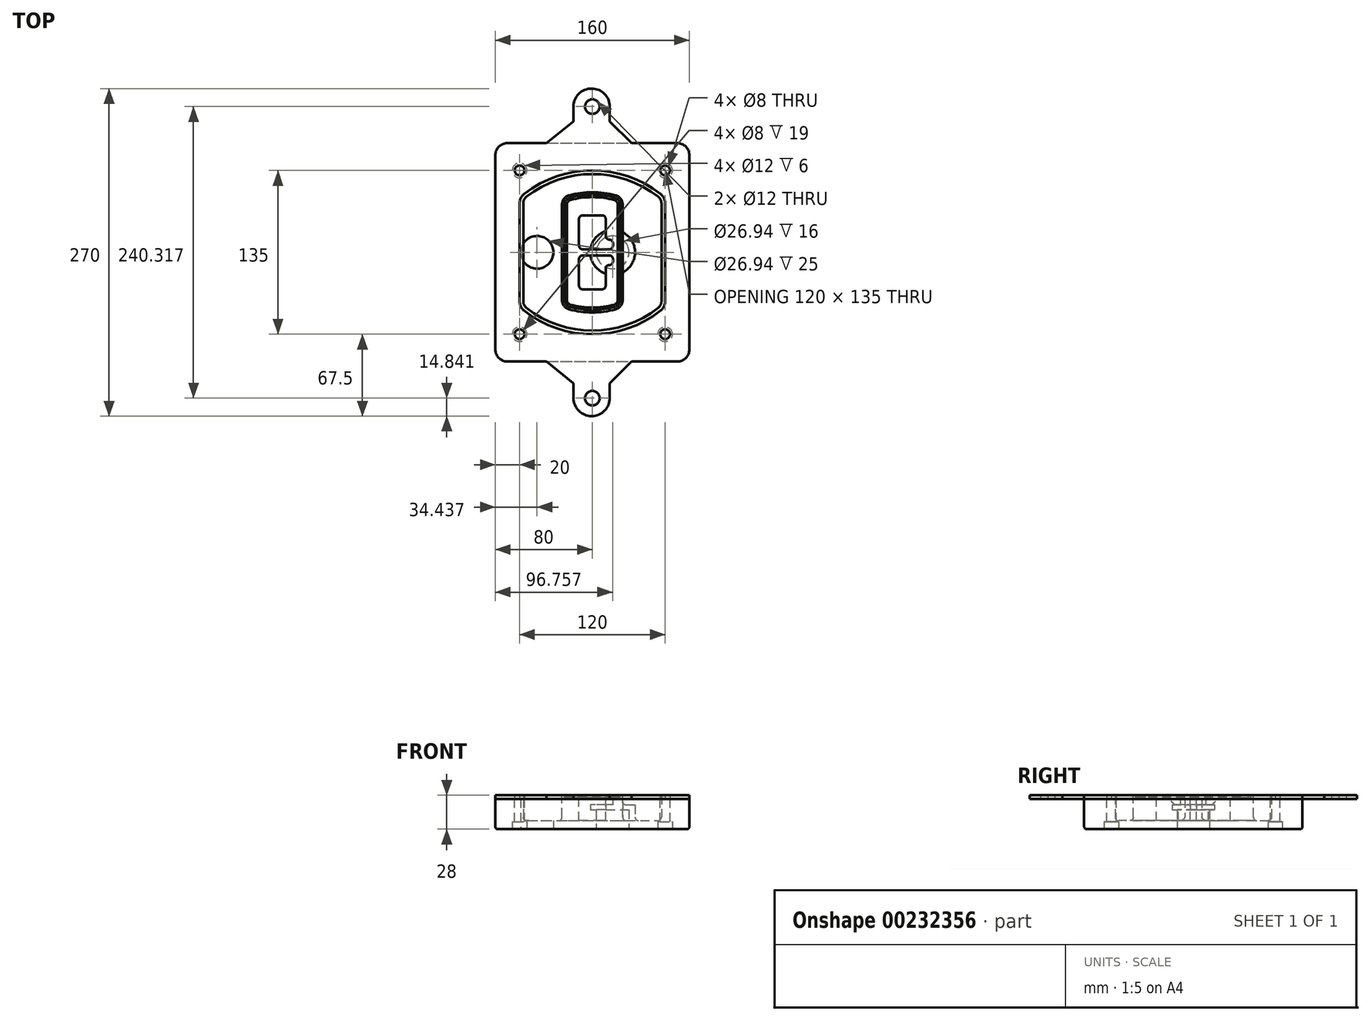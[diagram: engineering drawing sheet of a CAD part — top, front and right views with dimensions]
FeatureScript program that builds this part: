
annotation { "Feature Type Name" : "Feature", "Feature Type Description" : "" }
export const myFeature = defineFeature(function(context is Context, id is Id, definition is map)
    precondition{}
    {
        {
            var Q0;
            Q0=qCreatedBy(makeId("Top.planeOp"),FACE);
            var sketch = newSketch(context, id + "F0", { "sketchPlane" : qUnion([Q0])});
            skPoint(sketch, "E0.rect.middle", {"position": v(0, 0) * mm});
            skLineSegment(sketch, "E1.bottom", {"start": v(-70, -90) * mm, "end": v(70, -90) * mm});
            skLineSegment(sketch, "E1.top", {"start": v(-70, 90) * mm, "end": v(70, 90) * mm});
            skLineSegment(sketch, "E1.left", {"start": v(-80, -80) * mm, "end": v(-80, 80) * mm});
            skLineSegment(sketch, "E1.right", {"start": v(80, -80) * mm, "end": v(80, 80) * mm});
            skLineSegment(sketch, "E2", {"start": v(-80, 90) * mm, "end": v(80, -90) * mm, "construction": true});
            skLineSegment(sketch, "E3", {"start": v(80, 90) * mm, "end": v(-80, -90) * mm, "construction": true});
            skCircle(sketch, "E4", {"center": v(-60, 67.5) * mm, "radius": 4 * mm});
            skCircle(sketch, "E5", {"center": v(60, 67.5) * mm, "radius": 4 * mm});
            skCircle(sketch, "E6", {"center": v(60, -67.5) * mm, "radius": 4 * mm});
            skCircle(sketch, "E7", {"center": v(-60, -67.5) * mm, "radius": 4 * mm});
            skLineSegment(sketch, "E8", {"start": v(-60, 67.5) * mm, "end": v(60, 67.5) * mm, "construction": true});
            skLineSegment(sketch, "E9", {"start": v(60, 67.5) * mm, "end": v(60, -67.5) * mm, "construction": true});
            skLineSegment(sketch, "E10", {"start": v(60, -67.5) * mm, "end": v(-60, -67.5) * mm, "construction": true});
            skLineSegment(sketch, "E11", {"start": v(-60, -67.5) * mm, "end": v(-60, 67.5) * mm, "construction": true});
            skLineSegment(sketch, "E12", {"start": v(-60, 40.3) * mm, "end": v(-60, -40.3) * mm});
            skLineSegment(sketch, "E13", {"start": v(60, 40.3) * mm, "end": v(60, -40.3) * mm});
            skArc(sketch, "E14", {"start": v(56.15, 48.18) * mm, "mid": v(0, 67.5) * mm, "end": v(-56.15, 48.18) * mm});
            skArc(sketch, "E15", {"start": v(-56.15, -48.18) * mm, "mid": v(0, -67.5) * mm, "end": v(56.15, -48.18) * mm});
            skLineSegment(sketch, "E16", {"start": v(-60, 0) * mm, "end": v(60, 0) * mm, "construction": true});
            skPoint(sketch, "E17.visualSharp", {"position": v(-60, -45) * mm});
            skArc(sketch, "E17.filletArc", {"start": v(-60, -40.3) * mm, "mid": v(-58.99, -44.68) * mm, "end": v(-56.15, -48.18) * mm});
            skPoint(sketch, "E18.visualSharp", {"position": v(-60, 45) * mm});
            skArc(sketch, "E18.filletArc", {"start": v(-56.15, 48.18) * mm, "mid": v(-58.99, 44.68) * mm, "end": v(-60, 40.3) * mm});
            skPoint(sketch, "E19.visualSharp", {"position": v(60, 45) * mm});
            skArc(sketch, "E19.filletArc", {"start": v(60, 40.3) * mm, "mid": v(58.99, 44.68) * mm, "end": v(56.15, 48.18) * mm});
            skPoint(sketch, "E20.visualSharp", {"position": v(60, -45) * mm});
            skArc(sketch, "E20.filletArc", {"start": v(56.15, -48.18) * mm, "mid": v(58.99, -44.68) * mm, "end": v(60, -40.3) * mm});
            skPoint(sketch, "E21.visualSharp", {"position": v(-80, 90) * mm});
            skArc(sketch, "E21.filletArc", {"start": v(-70, 90) * mm, "mid": v(-77.07, 87.07) * mm, "end": v(-80, 80) * mm});
            skPoint(sketch, "E22.visualSharp", {"position": v(80, 90) * mm});
            skArc(sketch, "E22.filletArc", {"start": v(80, 80) * mm, "mid": v(77.07, 87.07) * mm, "end": v(70, 90) * mm});
            skPoint(sketch, "E23.visualSharp", {"position": v(80, -90) * mm});
            skArc(sketch, "E23.filletArc", {"start": v(70, -90) * mm, "mid": v(77.07, -87.07) * mm, "end": v(80, -80) * mm});
            skPoint(sketch, "E24.visualSharp", {"position": v(-80, -90) * mm});
            skArc(sketch, "E24.filletArc", {"start": v(-80, -80) * mm, "mid": v(-77.07, -87.07) * mm, "end": v(-70, -90) * mm});
            skArc(sketch, "E25.0", {"start": v(57, 40.3) * mm, "mid": v(56.3, 43.36) * mm, "end": v(54.3, 45.81) * mm});
            skLineSegment(sketch, "E25.1", {"start": v(57, 40.3) * mm, "end": v(57, -40.3) * mm});
            skArc(sketch, "E25.2", {"start": v(54.3, -45.81) * mm, "mid": v(56.3, -43.36) * mm, "end": v(57, -40.3) * mm});
            skArc(sketch, "E25.3", {"start": v(-54.3, -45.81) * mm, "mid": v(0, -64.5) * mm, "end": v(54.3, -45.81) * mm});
            skArc(sketch, "E25.4", {"start": v(-57, -40.3) * mm, "mid": v(-56.3, -43.36) * mm, "end": v(-54.3, -45.81) * mm});
            skArc(sketch, "E25.5", {"start": v(54.3, 45.81) * mm, "mid": v(0, 64.5) * mm, "end": v(-54.3, 45.81) * mm});
            skLineSegment(sketch, "E25.6", {"start": v(-57, 40.3) * mm, "end": v(-57, -40.3) * mm});
            skArc(sketch, "E25.7", {"start": v(-54.3, 45.81) * mm, "mid": v(-56.3, 43.36) * mm, "end": v(-57, 40.3) * mm});
            skArc(sketch, "E26.0", {"start": v(-58.62, 51.33) * mm, "mid": v(-62.58, 46.43) * mm, "end": v(-64, 40.3) * mm});
            skArc(sketch, "E26.1", {"start": v(58.62, 51.33) * mm, "mid": v(0, 71.5) * mm, "end": v(-58.62, 51.33) * mm});
            skArc(sketch, "E26.2", {"start": v(64, 40.3) * mm, "mid": v(62.58, 46.43) * mm, "end": v(58.62, 51.33) * mm});
            skLineSegment(sketch, "E26.3", {"start": v(64, 40.3) * mm, "end": v(64, -40.3) * mm});
            skArc(sketch, "E26.4", {"start": v(58.62, -51.33) * mm, "mid": v(62.58, -46.43) * mm, "end": v(64, -40.3) * mm});
            skLineSegment(sketch, "E26.5", {"start": v(-64, 40.3) * mm, "end": v(-64, -40.3) * mm});
            skArc(sketch, "E26.6", {"start": v(-58.62, -51.33) * mm, "mid": v(0, -71.5) * mm, "end": v(58.62, -51.33) * mm});
            skArc(sketch, "E26.7", {"start": v(-64, -40.3) * mm, "mid": v(-62.58, -46.43) * mm, "end": v(-58.62, -51.33) * mm});
            skSolve(sketch);
        }
        {
            var Q0;
            Q0=makeQuery(id+"F0.imprint","IMPRINT",FACE,{"disambiguationData":[TD([[makeQuery(id+"F0.imprint","IMPRINT",EDGE,{"derivedFrom":sQuery(id+"F0.wireOp",EDGE,"E1.bottom")}),1.0]])]});
            var Q1;
            Q1=makeQuery(id+"F0.imprint","IMPRINT",FACE,{"disambiguationData":[TD([[makeQuery(id+"F0.imprint","IMPRINT",EDGE,{"derivedFrom":sQuery(id+"F0.wireOp",EDGE,"E12")}),1.0]])]});
            var Q2;
            Q2=makeQuery(id+"F0.imprint","IMPRINT",FACE,{"disambiguationData":[TD([[makeQuery(id+"F0.imprint","IMPRINT",EDGE,{"derivedFrom":sQuery(id+"F0.wireOp",EDGE,"E25.0")}),1.0]])]});
            var Q3;
            Q3=makeQuery(id+"F0.imprint","IMPRINT",FACE,{"disambiguationData":[TD([[makeQuery(id+"F0.imprint","IMPRINT",EDGE,{"derivedFrom":sQuery(id+"F0.wireOp",EDGE,"E12")}),-1.0]])]});
            extrude(context, id + "F1", {"entities" : qUnion([Q0, Q1, Q2, Q3]), "oppositeDirection" : true, "depth" : 25 * mm});
        }
        {
            var Q0;
            Q0=makeQuery(id+"F0.imprint","IMPRINT",FACE,{"disambiguationData":[TD([[makeQuery(id+"F0.imprint","IMPRINT",EDGE,{"derivedFrom":sQuery(id+"F0.wireOp",EDGE,"E12")}),1.0]])]});
            extrude(context, id + "F2", {"entities" : qUnion([Q0]), "operationType" : NewBodyOperationType.ADD, "depth" : 3 * mm});
        }
        {
            var Q0;
            Q0=makeQuery(id+"F0.imprint","IMPRINT",FACE,{"disambiguationData":[TD([[makeQuery(id+"F0.imprint","IMPRINT",EDGE,{"derivedFrom":sQuery(id+"F0.wireOp",EDGE,"E25.0")}),1.0]])]});
            extrude(context, id + "F3", {"entities" : qUnion([Q0]), "operationType" : NewBodyOperationType.REMOVE, "oppositeDirection" : true, "depth" : 18 * mm});
        }
        {
            var Q0;
            Q0=makeQuery(id+"F2.opExtrude","CAP_FACE",FACE,{"disambiguationData":[OSD([sQuery(id+"F0.wireOp",EDGE,"E12"),sQuery(id+"F0.wireOp",EDGE,"E13"),sQuery(id+"F0.wireOp",EDGE,"E14"),sQuery(id+"F0.wireOp",EDGE,"E15"),sQuery(id+"F0.wireOp",EDGE,"E17.filletArc"),sQuery(id+"F0.wireOp",EDGE,"E18.filletArc"),sQuery(id+"F0.wireOp",EDGE,"E19.filletArc"),sQuery(id+"F0.wireOp",EDGE,"E20.filletArc"),sQuery(id+"F0.wireOp",EDGE,"E25.0"),sQuery(id+"F0.wireOp",EDGE,"E25.1"),sQuery(id+"F0.wireOp",EDGE,"E25.2"),sQuery(id+"F0.wireOp",EDGE,"E25.3"),sQuery(id+"F0.wireOp",EDGE,"E25.4"),sQuery(id+"F0.wireOp",EDGE,"E25.5"),sQuery(id+"F0.wireOp",EDGE,"E25.6"),sQuery(id+"F0.wireOp",EDGE,"E25.7")])],"isStart":false});
            var sketch = newSketch(context, id + "F4", { "sketchPlane" : qUnion([Q0])});
            skArc(sketch, "E27.0", {"start": v(-19.08, -46.97) * mm, "mid": v(0, -49.5) * mm, "end": v(19.08, -46.97) * mm});
            skArc(sketch, "E28.0", {"start": v(19.08, 46.97) * mm, "mid": v(0, 49.5) * mm, "end": v(-19.08, 46.97) * mm});
            skLineSegment(sketch, "E29", {"start": v(-25, 39.25) * mm, "end": v(-25, -39.25) * mm});
            skLineSegment(sketch, "E30", {"start": v(25, 39.25) * mm, "end": v(25, -39.25) * mm});
            skLineSegment(sketch, "E31", {"start": v(-25, 45.1) * mm, "end": v(25, 45.1) * mm, "construction": true});
            skLineSegment(sketch, "E32", {"start": v(-25, -45.1) * mm, "end": v(25, -45.1) * mm, "construction": true});
            skPoint(sketch, "E33.visualSharp", {"position": v(-25, 45.1) * mm});
            skArc(sketch, "E33.filletArc", {"start": v(-19.08, 46.97) * mm, "mid": v(-23.35, 44.11) * mm, "end": v(-25, 39.25) * mm});
            skPoint(sketch, "E34.visualSharp", {"position": v(25, 45.1) * mm});
            skArc(sketch, "E34.filletArc", {"start": v(25, 39.25) * mm, "mid": v(23.35, 44.11) * mm, "end": v(19.08, 46.97) * mm});
            skPoint(sketch, "E35.visualSharp", {"position": v(25, -45.1) * mm});
            skArc(sketch, "E35.filletArc", {"start": v(19.08, -46.97) * mm, "mid": v(23.35, -44.11) * mm, "end": v(25, -39.25) * mm});
            skPoint(sketch, "E36.visualSharp", {"position": v(-25, -45.1) * mm});
            skArc(sketch, "E36.filletArc", {"start": v(-25, -39.25) * mm, "mid": v(-23.35, -44.11) * mm, "end": v(-19.08, -46.97) * mm});
            skArc(sketch, "E37.0", {"start": v(54.3, 45.81) * mm, "mid": v(0, 64.5) * mm, "end": v(-54.3, 45.81) * mm});
            skArc(sketch, "E37.1", {"start": v(-54.3, 45.81) * mm, "mid": v(-56.3, 43.36) * mm, "end": v(-57, 40.3) * mm});
            skLineSegment(sketch, "E37.2", {"start": v(-57, 40.3) * mm, "end": v(-57, -40.3) * mm});
            skArc(sketch, "E37.3", {"start": v(-57, -40.3) * mm, "mid": v(-56.3, -43.36) * mm, "end": v(-54.3, -45.81) * mm});
            skArc(sketch, "E37.4", {"start": v(-54.3, -45.81) * mm, "mid": v(0, -64.5) * mm, "end": v(54.3, -45.81) * mm});
            skArc(sketch, "E37.5", {"start": v(54.3, -45.81) * mm, "mid": v(56.3, -43.36) * mm, "end": v(57, -40.3) * mm});
            skLineSegment(sketch, "E37.6", {"start": v(57, 40.3) * mm, "end": v(57, -40.3) * mm});
            skArc(sketch, "E37.7", {"start": v(57, 40.3) * mm, "mid": v(56.3, 43.36) * mm, "end": v(54.3, 45.81) * mm});
            skLineSegment(sketch, "E38.0", {"start": v(23, 39.25) * mm, "end": v(23, -39.25) * mm});
            skArc(sketch, "E38.1", {"start": v(18.56, -45.04) * mm, "mid": v(21.76, -42.9) * mm, "end": v(23, -39.25) * mm});
            skArc(sketch, "E38.2", {"start": v(-18.56, -45.04) * mm, "mid": v(0, -47.5) * mm, "end": v(18.56, -45.04) * mm});
            skArc(sketch, "E38.3", {"start": v(-23, -39.25) * mm, "mid": v(-21.76, -42.9) * mm, "end": v(-18.56, -45.04) * mm});
            skLineSegment(sketch, "E38.4", {"start": v(-23, 39.25) * mm, "end": v(-23, -39.25) * mm});
            skArc(sketch, "E38.5", {"start": v(23, 39.25) * mm, "mid": v(21.76, 42.9) * mm, "end": v(18.56, 45.04) * mm});
            skArc(sketch, "E38.6", {"start": v(-18.56, 45.04) * mm, "mid": v(-21.76, 42.9) * mm, "end": v(-23, 39.25) * mm});
            skArc(sketch, "E38.7", {"start": v(18.56, 45.04) * mm, "mid": v(0, 47.5) * mm, "end": v(-18.56, 45.04) * mm});
            skArc(sketch, "E39.0", {"start": v(21, 39.25) * mm, "mid": v(20.18, 41.68) * mm, "end": v(18.04, 43.1) * mm});
            skLineSegment(sketch, "E39.1", {"start": v(21, 39.25) * mm, "end": v(21, -39.25) * mm});
            skArc(sketch, "E39.2", {"start": v(18.04, -43.1) * mm, "mid": v(20.18, -41.68) * mm, "end": v(21, -39.25) * mm});
            skArc(sketch, "E39.3", {"start": v(-18.04, -43.1) * mm, "mid": v(0, -45.5) * mm, "end": v(18.04, -43.1) * mm});
            skArc(sketch, "E39.4", {"start": v(-21, -39.25) * mm, "mid": v(-20.18, -41.68) * mm, "end": v(-18.04, -43.1) * mm});
            skArc(sketch, "E39.5", {"start": v(18.04, 43.1) * mm, "mid": v(0, 45.5) * mm, "end": v(-18.04, 43.1) * mm});
            skLineSegment(sketch, "E39.6", {"start": v(-21, 39.25) * mm, "end": v(-21, -39.25) * mm});
            skArc(sketch, "E39.7", {"start": v(-18.04, 43.1) * mm, "mid": v(-20.18, 41.68) * mm, "end": v(-21, 39.25) * mm});
            skLineSegment(sketch, "E40", {"start": v(-25, 0) * mm, "end": v(25, 0) * mm, "construction": true});
            skLineSegment(sketch, "E41", {"start": v(-11, 5.5) * mm, "end": v(-11, 27.5) * mm});
            skLineSegment(sketch, "E42", {"start": v(-8, 30.5) * mm, "end": v(8, 30.5) * mm});
            skLineSegment(sketch, "E43", {"start": v(11, 27.5) * mm, "end": v(11, 13.5) * mm});
            skLineSegment(sketch, "E44", {"start": v(14, 10.5) * mm, "end": v(14, 10.5) * mm});
            skLineSegment(sketch, "E45", {"start": v(17, 7.5) * mm, "end": v(17, 5.5) * mm});
            skLineSegment(sketch, "E46", {"start": v(14, 2.5) * mm, "end": v(-8, 2.5) * mm});
            skPoint(sketch, "E47.visualSharp", {"position": v(-11, 30.5) * mm});
            skArc(sketch, "E47.filletArc", {"start": v(-8, 30.5) * mm, "mid": v(-10.12, 29.62) * mm, "end": v(-11, 27.5) * mm});
            skPoint(sketch, "E48.visualSharp", {"position": v(11, 30.5) * mm});
            skArc(sketch, "E48.filletArc", {"start": v(11, 27.5) * mm, "mid": v(10.12, 29.62) * mm, "end": v(8, 30.5) * mm});
            skPoint(sketch, "E49.visualSharp", {"position": v(11, 10.5) * mm});
            skArc(sketch, "E49.filletArc", {"start": v(11, 13.5) * mm, "mid": v(11.88, 11.38) * mm, "end": v(14, 10.5) * mm});
            skPoint(sketch, "E50.visualSharp", {"position": v(17, 10.5) * mm});
            skArc(sketch, "E50.filletArc", {"start": v(17, 7.5) * mm, "mid": v(16.12, 9.62) * mm, "end": v(14, 10.5) * mm});
            skPoint(sketch, "E51.visualSharp", {"position": v(17, 2.5) * mm});
            skArc(sketch, "E51.filletArc", {"start": v(14, 2.5) * mm, "mid": v(16.12, 3.38) * mm, "end": v(17, 5.5) * mm});
            skPoint(sketch, "E52.visualSharp", {"position": v(-11, 2.5) * mm});
            skArc(sketch, "E52.filletArc", {"start": v(-11, 5.5) * mm, "mid": v(-10.12, 3.38) * mm, "end": v(-8, 2.5) * mm});
            skLineSegment(sketch, "E53.0.MirrorCS", {"start": v(14, -2.5) * mm, "end": v(-8, -2.5) * mm});
            skArc(sketch, "E54.0.MirrorCS", {"start": v(-11, -5.5) * mm, "mid": v(-10.12, -3.38) * mm, "end": v(-8, -2.5) * mm});
            skLineSegment(sketch, "E55.0.MirrorCS", {"start": v(-11, -5.5) * mm, "end": v(-11, -27.5) * mm});
            skArc(sketch, "E56.0.MirrorCS", {"start": v(-8, -30.5) * mm, "mid": v(-10.12, -29.62) * mm, "end": v(-11, -27.5) * mm});
            skLineSegment(sketch, "E57.0.MirrorCS", {"start": v(-8, -30.5) * mm, "end": v(8, -30.5) * mm});
            skArc(sketch, "E58.0.MirrorCS", {"start": v(11, -27.5) * mm, "mid": v(10.12, -29.62) * mm, "end": v(8, -30.5) * mm});
            skLineSegment(sketch, "E59.0.MirrorCS", {"start": v(11, -27.5) * mm, "end": v(11, -13.5) * mm});
            skArc(sketch, "E60.0.MirrorCS", {"start": v(11, -13.5) * mm, "mid": v(11.88, -11.38) * mm, "end": v(14, -10.5) * mm});
            skArc(sketch, "E61.0.MirrorCS", {"start": v(17, -7.5) * mm, "mid": v(16.12, -9.62) * mm, "end": v(14, -10.5) * mm});
            skLineSegment(sketch, "E62.0.MirrorCS", {"start": v(17, -7.5) * mm, "end": v(17, -5.5) * mm});
            skArc(sketch, "E63.0.MirrorCS", {"start": v(14, -2.5) * mm, "mid": v(16.12, -3.38) * mm, "end": v(17, -5.5) * mm});
            skSolve(sketch);
        }
        {
            var Q0;
            Q0=makeQuery(id+"F4.imprint","IMPRINT",FACE,{"disambiguationData":[TD([[makeQuery(id+"F4.imprint","IMPRINT",EDGE,{"derivedFrom":sQuery(id+"F4.wireOp",EDGE,"E27.0")}),1.0]])]});
            var Q1;
            Q1=makeQuery(id+"F4.imprint","IMPRINT",FACE,{"disambiguationData":[TD([[makeQuery(id+"F4.imprint","IMPRINT",EDGE,{"derivedFrom":sQuery(id+"F4.wireOp",EDGE,"E38.0")}),-1.0]])]});
            var Q2;
            Q2=makeQuery(id+"F4.imprint","IMPRINT",FACE,{"disambiguationData":[TD([[makeQuery(id+"F4.imprint","IMPRINT",EDGE,{"derivedFrom":sQuery(id+"F4.wireOp",EDGE,"E39.0")}),1.0]])]});
            extrude(context, id + "F5", {"entities" : qUnion([Q0, Q1, Q2]), "operationType" : NewBodyOperationType.ADD, "endBound" : BoundingType.UP_TO_NEXT, "oppositeDirection" : true, "depth" : 25 * mm});
        }
        {
            var Q0;
            Q0=makeQuery(id+"F4.imprint","IMPRINT",FACE,{"disambiguationData":[TD([[makeQuery(id+"F4.imprint","IMPRINT",EDGE,{"derivedFrom":sQuery(id+"F4.wireOp",EDGE,"E38.0")}),-1.0]])]});
            extrude(context, id + "F6", {"entities" : qUnion([Q0]), "operationType" : NewBodyOperationType.REMOVE, "oppositeDirection" : true, "depth" : 2 * mm});
        }
        {
            var Q0;
            Q0=makeQuery(id+"F1.opExtrude","CAP_FACE",FACE,{"disambiguationData":[OSD([sQuery(id+"F0.wireOp",EDGE,"E1.bottom"),sQuery(id+"F0.wireOp",EDGE,"E1.top"),sQuery(id+"F0.wireOp",EDGE,"E1.left"),sQuery(id+"F0.wireOp",EDGE,"E1.right"),sQuery(id+"F0.wireOp",EDGE,"E4"),sQuery(id+"F0.wireOp",EDGE,"E5"),sQuery(id+"F0.wireOp",EDGE,"E6"),sQuery(id+"F0.wireOp",EDGE,"E7"),sQuery(id+"F0.wireOp",EDGE,"E21.filletArc"),sQuery(id+"F0.wireOp",EDGE,"E22.filletArc"),sQuery(id+"F0.wireOp",EDGE,"E23.filletArc"),sQuery(id+"F0.wireOp",EDGE,"E24.filletArc")])],"isStart":false});
            var sketch = newSketch(context, id + "F7", { "sketchPlane" : qUnion([Q0])});
            skCircle(sketch, "E64", {"center": v(16.76, 0) * mm, "radius": 13.47 * mm});
            skCircle(sketch, "E65", {"center": v(-45.56, 0) * mm, "radius": 13.47 * mm});
            skLineSegment(sketch, "E66", {"start": v(80, 0) * mm, "end": v(-80, 0) * mm});
            skCircle(sketch, "E67", {"center": v(16.76, 0) * mm, "radius": 18.47 * mm});
            skCircle(sketch, "E68", {"center": v(60, -67.5) * mm, "radius": 6 * mm});
            skCircle(sketch, "E69", {"center": v(-60, -67.5) * mm, "radius": 6 * mm});
            skCircle(sketch, "E70", {"center": v(-60, 67.5) * mm, "radius": 6 * mm});
            skCircle(sketch, "E71", {"center": v(60, 67.5) * mm, "radius": 6 * mm});
            skSolve(sketch);
        }
        {
            var Q0;
            {var subQ1=sQuery(id+"F7.wireOp",EDGE,"E66");var subQ4=sQuery(id+"F7.wireOp",EDGE,"E64");var subQ6=makeQuery(id+"F7.imprint","INTERSECT",VERTEX,{"disambiguationData":[OD(0.0)],"derivedFrom":[subQ4,subQ1]});Q0=makeQuery(id+"F7.imprint","IMPRINT",FACE,{"disambiguationData":[TD([[makeQuery(id+"F7.imprint","IMPRINT",EDGE,{"disambiguationData":[TD([[subQ6,-1.0]])],"derivedFrom":subQ4}),-1.0]])]});}
            var Q1;
            {var subQ0=sQuery(id+"F7.wireOp",EDGE,"E66");var subQ1=sQuery(id+"F7.wireOp",EDGE,"E64");var subQ3=makeQuery(id+"F7.imprint","INTERSECT",VERTEX,{"disambiguationData":[OD(0.0)],"derivedFrom":[subQ1,subQ0]});Q1=makeQuery(id+"F7.imprint","IMPRINT",FACE,{"disambiguationData":[TD([[makeQuery(id+"F7.imprint","IMPRINT",EDGE,{"disambiguationData":[TD([[subQ3,-1.0]])],"derivedFrom":subQ1}),1.0]])]});}
            var Q2;
            {var subQ0=sQuery(id+"F7.wireOp",EDGE,"E66");var subQ1=sQuery(id+"F7.wireOp",EDGE,"E64");var subQ3=makeQuery(id+"F7.imprint","INTERSECT",VERTEX,{"disambiguationData":[OD(0.0)],"derivedFrom":[subQ1,subQ0]});Q2=makeQuery(id+"F7.imprint","IMPRINT",FACE,{"disambiguationData":[TD([[makeQuery(id+"F7.imprint","IMPRINT",EDGE,{"disambiguationData":[TD([[subQ3,1.0]])],"derivedFrom":subQ1}),1.0]])]});}
            var Q3;
            {var subQ1=sQuery(id+"F7.wireOp",EDGE,"E66");var subQ4=sQuery(id+"F7.wireOp",EDGE,"E64");var subQ6=makeQuery(id+"F7.imprint","INTERSECT",VERTEX,{"disambiguationData":[OD(0.0)],"derivedFrom":[subQ4,subQ1]});Q3=makeQuery(id+"F7.imprint","IMPRINT",FACE,{"disambiguationData":[TD([[makeQuery(id+"F7.imprint","IMPRINT",EDGE,{"disambiguationData":[TD([[subQ6,1.0]])],"derivedFrom":subQ4}),-1.0]])]});}
            extrude(context, id + "F8", {"entities" : qUnion([Q0, Q1, Q2, Q3]), "operationType" : NewBodyOperationType.ADD, "oppositeDirection" : true, "depth" : 20 * mm});
        }
        {
            var Q0;
            {var subQ0=sQuery(id+"F7.wireOp",EDGE,"E66");var subQ1=sQuery(id+"F7.wireOp",EDGE,"E64");var subQ3=makeQuery(id+"F7.imprint","INTERSECT",VERTEX,{"disambiguationData":[OD(0.0)],"derivedFrom":[subQ1,subQ0]});Q0=makeQuery(id+"F7.imprint","IMPRINT",FACE,{"disambiguationData":[TD([[makeQuery(id+"F7.imprint","IMPRINT",EDGE,{"disambiguationData":[TD([[subQ3,-1.0]])],"derivedFrom":subQ1}),1.0]])]});}
            var Q1;
            {var subQ0=sQuery(id+"F7.wireOp",EDGE,"E66");var subQ1=sQuery(id+"F7.wireOp",EDGE,"E64");var subQ3=makeQuery(id+"F7.imprint","INTERSECT",VERTEX,{"disambiguationData":[OD(0.0)],"derivedFrom":[subQ1,subQ0]});Q1=makeQuery(id+"F7.imprint","IMPRINT",FACE,{"disambiguationData":[TD([[makeQuery(id+"F7.imprint","IMPRINT",EDGE,{"disambiguationData":[TD([[subQ3,1.0]])],"derivedFrom":subQ1}),1.0]])]});}
            extrude(context, id + "F9", {"entities" : qUnion([Q0, Q1]), "operationType" : NewBodyOperationType.REMOVE, "oppositeDirection" : true, "depth" : 16 * mm});
        }
        {
            var Q0;
            {var subQ0=sQuery(id+"F7.wireOp",EDGE,"E66");var subQ1=sQuery(id+"F7.wireOp",EDGE,"E65");var subQ3=makeQuery(id+"F7.imprint","INTERSECT",VERTEX,{"disambiguationData":[OD(0.0)],"derivedFrom":[subQ1,subQ0]});Q0=makeQuery(id+"F7.imprint","IMPRINT",FACE,{"disambiguationData":[TD([[makeQuery(id+"F7.imprint","IMPRINT",EDGE,{"disambiguationData":[TD([[subQ3,-1.0]])],"derivedFrom":subQ1}),1.0]])]});}
            var Q1;
            {var subQ0=sQuery(id+"F7.wireOp",EDGE,"E66");var subQ1=sQuery(id+"F7.wireOp",EDGE,"E65");var subQ3=makeQuery(id+"F7.imprint","INTERSECT",VERTEX,{"disambiguationData":[OD(0.0)],"derivedFrom":[subQ1,subQ0]});Q1=makeQuery(id+"F7.imprint","IMPRINT",FACE,{"disambiguationData":[TD([[makeQuery(id+"F7.imprint","IMPRINT",EDGE,{"disambiguationData":[TD([[subQ3,1.0]])],"derivedFrom":subQ1}),1.0]])]});}
            extrude(context, id + "F10", {"entities" : qUnion([Q0, Q1]), "operationType" : NewBodyOperationType.REMOVE, "oppositeDirection" : true, "depth" : 25 * mm});
        }
        {
            var Q0;
            Q0=makeQuery(id+"F7.imprint","IMPRINT",FACE,{"disambiguationData":[TD([[makeQuery(id+"F7.imprint","IMPRINT",EDGE,{"derivedFrom":sQuery(id+"F7.wireOp",EDGE,"E68")}),1.0]])]});
            var Q1;
            Q1=makeQuery(id+"F7.imprint","IMPRINT",FACE,{"disambiguationData":[TD([[makeQuery(id+"F7.imprint","IMPRINT",EDGE,{"derivedFrom":makeQuery(id+"F1.opExtrude","CAP_EDGE",EDGE,{"disambiguationData":[OSD([sQuery(id+"F0.wireOp",EDGE,"E5")])],"isStart":false})}),-1.0]])]});
            var Q2;
            Q2=makeQuery(id+"F7.imprint","IMPRINT",FACE,{"disambiguationData":[TD([[makeQuery(id+"F7.imprint","IMPRINT",EDGE,{"derivedFrom":sQuery(id+"F7.wireOp",EDGE,"E69")}),1.0]])]});
            var Q3;
            Q3=makeQuery(id+"F7.imprint","IMPRINT",FACE,{"disambiguationData":[TD([[makeQuery(id+"F7.imprint","IMPRINT",EDGE,{"derivedFrom":makeQuery(id+"F1.opExtrude","CAP_EDGE",EDGE,{"disambiguationData":[OSD([sQuery(id+"F0.wireOp",EDGE,"E4")])],"isStart":false})}),-1.0]])]});
            var Q4;
            Q4=makeQuery(id+"F7.imprint","IMPRINT",FACE,{"disambiguationData":[TD([[makeQuery(id+"F7.imprint","IMPRINT",EDGE,{"derivedFrom":sQuery(id+"F7.wireOp",EDGE,"E70")}),1.0]])]});
            var Q5;
            Q5=makeQuery(id+"F7.imprint","IMPRINT",FACE,{"disambiguationData":[TD([[makeQuery(id+"F7.imprint","IMPRINT",EDGE,{"derivedFrom":makeQuery(id+"F1.opExtrude","CAP_EDGE",EDGE,{"disambiguationData":[OSD([sQuery(id+"F0.wireOp",EDGE,"E7")])],"isStart":false})}),-1.0]])]});
            var Q6;
            Q6=makeQuery(id+"F7.imprint","IMPRINT",FACE,{"disambiguationData":[TD([[makeQuery(id+"F7.imprint","IMPRINT",EDGE,{"derivedFrom":sQuery(id+"F7.wireOp",EDGE,"E71")}),1.0]])]});
            var Q7;
            Q7=makeQuery(id+"F7.imprint","IMPRINT",FACE,{"disambiguationData":[TD([[makeQuery(id+"F7.imprint","IMPRINT",EDGE,{"derivedFrom":makeQuery(id+"F1.opExtrude","CAP_EDGE",EDGE,{"disambiguationData":[OSD([sQuery(id+"F0.wireOp",EDGE,"E6")])],"isStart":false})}),-1.0]])]});
            extrude(context, id + "F11", {"entities" : qUnion([Q0, Q1, Q2, Q3, Q4, Q5, Q6, Q7]), "operationType" : NewBodyOperationType.REMOVE, "oppositeDirection" : true, "depth" : 6 * mm});
        }
        {
            var Q0;
            Q0=makeQuery(id+"F9.boolean.opBoolean","COPY",FACE,{"derivedFrom":makeQuery(id+"F9.opExtrude","CAP_FACE",FACE,{"disambiguationData":[OSD([sQuery(id+"F7.wireOp",EDGE,"E64")])],"isStart":false})});
            var sketch = newSketch(context, id + "F12", { "sketchPlane" : qUnion([Q0])});
            skArc(sketch, "E72.0", {"start": v(11, 17.55) * mm, "mid": v(2.57, 11.82) * mm, "end": v(-1.54, 2.5) * mm});
            skArc(sketch, "E72.1", {"start": v(-1.54, -2.5) * mm, "mid": v(2.57, -11.82) * mm, "end": v(11, -17.55) * mm});
            skLineSegment(sketch, "E73", {"start": v(-1.54, -2.5) * mm, "end": v(14, -2.5) * mm});
            skLineSegment(sketch, "E74.0", {"start": v(14, 2.5) * mm, "end": v(-1.54, 2.5) * mm});
            skArc(sketch, "E74.1", {"start": v(14, 2.5) * mm, "mid": v(16.12, 3.38) * mm, "end": v(17, 5.5) * mm});
            skLineSegment(sketch, "E74.2", {"start": v(17, 7.5) * mm, "end": v(17, 5.5) * mm});
            skArc(sketch, "E74.3", {"start": v(17, 7.5) * mm, "mid": v(16.12, 9.62) * mm, "end": v(14, 10.5) * mm});
            skArc(sketch, "E74.4", {"start": v(11, 13.5) * mm, "mid": v(11.88, 11.38) * mm, "end": v(14, 10.5) * mm});
            skLineSegment(sketch, "E74.5", {"start": v(11, 17.55) * mm, "end": v(11, 13.5) * mm});
            skLineSegment(sketch, "E74.7", {"start": v(14, -2.5) * mm, "end": v(-1.54, -2.5) * mm});
            skArc(sketch, "E74.8", {"start": v(14, -2.5) * mm, "mid": v(16.12, -3.38) * mm, "end": v(17, -5.5) * mm});
            skLineSegment(sketch, "E74.9", {"start": v(17, -7.5) * mm, "end": v(17, -5.5) * mm});
            skArc(sketch, "E74.10", {"start": v(17, -7.5) * mm, "mid": v(16.12, -9.62) * mm, "end": v(14, -10.5) * mm});
            skArc(sketch, "E74.11", {"start": v(11, -13.5) * mm, "mid": v(11.88, -11.38) * mm, "end": v(14, -10.5) * mm});
            skLineSegment(sketch, "E74.12", {"start": v(11, -17.55) * mm, "end": v(11, -13.5) * mm});
            skPoint(sketch, "E75.orphan", {"position": v(11, -27.5) * mm});
            skPoint(sketch, "E76.orphan", {"position": v(-8, -2.5) * mm});
            skPoint(sketch, "E77.orphan", {"position": v(-8, 2.5) * mm});
            skPoint(sketch, "E78.orphan", {"position": v(11, 27.5) * mm});
            skSolve(sketch);
        }
        {
            var Q0;
            {var subQ7=sQuery(id+"F12.wireOp",EDGE,"E72.0");var subQ14=sQuery(id+"F12.wireOp",EDGE,"E72.1");var subQ16=sQuery(id+"F12.wireOp",EDGE,"E74.1");var subQ18=sQuery(id+"F12.wireOp",EDGE,"E74.8");Q0=qUnion([makeQuery(id+"F12.imprint","IMPRINT",FACE,{"disambiguationData":[TD([[makeQuery(id+"F12.imprint","IMPRINT",EDGE,{"derivedFrom":subQ7}),1.0]])]}),makeQuery(id+"F12.imprint","IMPRINT",FACE,{"disambiguationData":[TD([[makeQuery(id+"F12.imprint","IMPRINT",EDGE,{"derivedFrom":subQ14}),1.0]])]}),makeQuery(id+"F12.imprint","IMPRINT",FACE,{"disambiguationData":[TD([[makeQuery(id+"F12.imprint","IMPRINT",EDGE,{"derivedFrom":subQ16}),1.0]])]}),makeQuery(id+"F12.imprint","IMPRINT",FACE,{"disambiguationData":[TD([[makeQuery(id+"F12.imprint","IMPRINT",EDGE,{"derivedFrom":subQ18}),-1.0]])]})]);}
            var Q1;
            Q1=makeQuery(id+"F5.boolean.opBoolean","SPLIT",FACE,{"disambiguationData":[TD([makeQuery(id+"F5.opExtrude","SWEPT_FACE",FACE,{"disambiguationData":[OSD([sQuery(id+"F4.wireOp",EDGE,"E41")])]})])],"derivedFrom":makeQuery(id+"F3.boolean.opBoolean","COPY",FACE,{"derivedFrom":makeQuery(id+"F3.opExtrude","CAP_FACE",FACE,{"disambiguationData":[OSD([sQuery(id+"F0.wireOp",EDGE,"E25.0"),sQuery(id+"F0.wireOp",EDGE,"E25.1"),sQuery(id+"F0.wireOp",EDGE,"E25.2"),sQuery(id+"F0.wireOp",EDGE,"E25.3"),sQuery(id+"F0.wireOp",EDGE,"E25.4"),sQuery(id+"F0.wireOp",EDGE,"E25.5"),sQuery(id+"F0.wireOp",EDGE,"E25.6"),sQuery(id+"F0.wireOp",EDGE,"E25.7")])],"isStart":false})})});
            extrude(context, id + "F13", {"entities" : qUnion([Q0]), "operationType" : NewBodyOperationType.REMOVE, "endBound" : BoundingType.UP_TO_SURFACE, "endBoundEntityFace" : qUnion([Q1]), "depth" : 25 * mm});
        }
        {
            var Q0;
            Q0=makeQuery(id+"F3.boolean.opBoolean","COPY",EDGE,{"derivedFrom":makeQuery(id+"F3.opExtrude","CAP_EDGE",EDGE,{"disambiguationData":[OSD([sQuery(id+"F0.wireOp",EDGE,"E25.6")])],"isStart":false})});
            var Q1;
            Q1=makeQuery(id+"F8.boolean.opBoolean","INTERSECT",EDGE,{"derivedFrom":[makeQuery(id+"F5.opExtrude","SWEPT_FACE",FACE,{"disambiguationData":[OSD([sQuery(id+"F4.wireOp",EDGE,"E30")])]}),makeQuery(id+"F8.opExtrude","CAP_FACE",FACE,{"disambiguationData":[OSD([sQuery(id+"F7.wireOp",EDGE,"E67")])],"isStart":false})]});
            var Q2;
            Q2=makeQuery(id+"F8.boolean.opBoolean","INTERSECT",EDGE,{"disambiguationData":[OD(1.0)],"derivedFrom":[makeQuery(id+"F5.opExtrude","SWEPT_FACE",FACE,{"disambiguationData":[OSD([sQuery(id+"F4.wireOp",EDGE,"E30")])]}),makeQuery(id+"F8.opExtrude","SWEPT_FACE",FACE,{"disambiguationData":[OSD([sQuery(id+"F7.wireOp",EDGE,"E67")])]})]});
            var Q3;
            {var subQ0=sQuery(id+"F4.wireOp",EDGE,"E30");Q3=makeQuery(id+"F8.boolean.opBoolean","SPLIT",EDGE,{"disambiguationData":[TD([makeQuery(id+"F5.opExtrude","SWEPT_FACE",FACE,{"disambiguationData":[OSD([sQuery(id+"F4.wireOp",EDGE,"E35.filletArc")])]})])],"derivedFrom":makeQuery(id+"F5.opExtrude","CAP_EDGE",EDGE,{"disambiguationData":[OSD([subQ0])],"isStart":false})});}
            var Q4;
            {var subQ0=sQuery(id+"F0.wireOp",EDGE,"E25.7");var subQ1=sQuery(id+"F0.wireOp",EDGE,"E25.1");var subQ2=sQuery(id+"F0.wireOp",EDGE,"E25.6");var subQ3=sQuery(id+"F0.wireOp",EDGE,"E25.5");var subQ4=sQuery(id+"F0.wireOp",EDGE,"E25.4");var subQ5=sQuery(id+"F0.wireOp",EDGE,"E25.0");var subQ6=sQuery(id+"F0.wireOp",EDGE,"E25.2");var subQ7=sQuery(id+"F0.wireOp",EDGE,"E25.3");Q4=makeQuery(id+"F8.boolean.opBoolean","INTERSECT",EDGE,{"derivedFrom":[makeQuery(id+"F5.boolean.opBoolean","SPLIT",FACE,{"disambiguationData":[TD([makeQuery(id+"F2.opExtrude","SWEPT_FACE",FACE,{"disambiguationData":[OSD([subQ5])]})])],"derivedFrom":makeQuery(id+"F3.boolean.opBoolean","COPY",FACE,{"derivedFrom":makeQuery(id+"F3.opExtrude","CAP_FACE",FACE,{"disambiguationData":[OSD([subQ5,subQ1,subQ6,subQ7,subQ4,subQ3,subQ2,subQ0])],"isStart":false})})}),makeQuery(id+"F8.opExtrude","SWEPT_FACE",FACE,{"disambiguationData":[OSD([sQuery(id+"F7.wireOp",EDGE,"E67")])]})]});}
            var Q5;
            Q5=makeQuery(id+"F8.boolean.opBoolean","INTERSECT",EDGE,{"disambiguationData":[OD(0.0)],"derivedFrom":[makeQuery(id+"F5.opExtrude","SWEPT_FACE",FACE,{"disambiguationData":[OSD([sQuery(id+"F4.wireOp",EDGE,"E30")])]}),makeQuery(id+"F8.opExtrude","SWEPT_FACE",FACE,{"disambiguationData":[OSD([sQuery(id+"F7.wireOp",EDGE,"E67")])]})]});
            fillet(context, id + "F14", {"entities" : qUnion([Q0, Q1, Q2, Q3, Q4, Q5]), "radius" : 3 * mm, "tangentPropagation" : true, "allowEdgeOverflow" : false});
        }
        {
            var Q0;
            Q0=makeQuery(id+"F1.opExtrude","CAP_EDGE",EDGE,{"disambiguationData":[OSD([sQuery(id+"F0.wireOp",EDGE,"E1.bottom")])],"isStart":false});
            fillet(context, id + "F15", {"entities" : qUnion([Q0]), "radius" : 2 * mm, "tangentPropagation" : true, "allowEdgeOverflow" : false});
        }
        {
            var Q0;
            {var subQ0=sQuery(id+"F0.wireOp",EDGE,"E22.filletArc");var subQ1=sQuery(id+"F0.wireOp",EDGE,"E7");var subQ2=sQuery(id+"F0.wireOp",EDGE,"E6");var subQ3=sQuery(id+"F0.wireOp",EDGE,"E5");var subQ4=sQuery(id+"F0.wireOp",EDGE,"E4");var subQ5=sQuery(id+"F0.wireOp",EDGE,"E1.bottom");var subQ6=sQuery(id+"F0.wireOp",EDGE,"E21.filletArc");var subQ7=sQuery(id+"F0.wireOp",EDGE,"E1.top");var subQ8=sQuery(id+"F0.wireOp",EDGE,"E1.left");var subQ9=sQuery(id+"F0.wireOp",EDGE,"E1.right");var subQ10=sQuery(id+"F0.wireOp",EDGE,"E23.filletArc");var subQ11=sQuery(id+"F0.wireOp",EDGE,"E24.filletArc");Q0=makeQuery(id+"F2.boolean.opBoolean","SPLIT",FACE,{"disambiguationData":[TD([makeQuery(id+"F1.opExtrude","SWEPT_FACE",FACE,{"disambiguationData":[OSD([subQ5])]})])],"derivedFrom":makeQuery(id+"F1.opExtrude","CAP_FACE",FACE,{"disambiguationData":[OSD([subQ5,subQ7,subQ8,subQ9,subQ4,subQ3,subQ2,subQ1,subQ6,subQ0,subQ10,subQ11])],"isStart":true})});}
            var sketch = newSketch(context, id + "F16", { "sketchPlane" : qUnion([Q0])});
            skCircle(sketch, "E79.0", {"center": v(-60, 67.5) * mm, "radius": 4 * mm});
            skCircle(sketch, "E79.1", {"center": v(60, -67.5) * mm, "radius": 4 * mm});
            skCircle(sketch, "E79.2", {"center": v(60, 67.5) * mm, "radius": 4 * mm});
            skCircle(sketch, "E79.3", {"center": v(-60, -67.5) * mm, "radius": 4 * mm});
            skArc(sketch, "E79.4", {"start": v(56.15, 48.18) * mm, "mid": v(0, 67.5) * mm, "end": v(-56.15, 48.18) * mm});
            skArc(sketch, "E79.5", {"start": v(-56.15, 48.18) * mm, "mid": v(-58.99, 44.68) * mm, "end": v(-60, 40.3) * mm});
            skLineSegment(sketch, "E79.6", {"start": v(-60, 40.3) * mm, "end": v(-60, -40.3) * mm});
            skLineSegment(sketch, "E79.7", {"start": v(60, 40.3) * mm, "end": v(60, -40.3) * mm});
            skArc(sketch, "E79.8", {"start": v(60, 40.3) * mm, "mid": v(58.99, 44.68) * mm, "end": v(56.15, 48.18) * mm});
            skArc(sketch, "E79.9", {"start": v(-56.15, -48.18) * mm, "mid": v(0, -67.5) * mm, "end": v(56.15, -48.18) * mm});
            skArc(sketch, "E79.10", {"start": v(56.15, -48.18) * mm, "mid": v(58.99, -44.68) * mm, "end": v(60, -40.3) * mm});
            skArc(sketch, "E79.11", {"start": v(-60, -40.3) * mm, "mid": v(-58.99, -44.68) * mm, "end": v(-56.15, -48.18) * mm});
            skLineSegment(sketch, "E79.12", {"start": v(-70, 90) * mm, "end": v(70, 90) * mm});
            skArc(sketch, "E79.13", {"start": v(-70, 90) * mm, "mid": v(-77.07, 87.07) * mm, "end": v(-80, 80) * mm});
            skLineSegment(sketch, "E79.14", {"start": v(-80, -80) * mm, "end": v(-80, 80) * mm});
            skArc(sketch, "E79.15", {"start": v(80, 80) * mm, "mid": v(77.07, 87.07) * mm, "end": v(70, 90) * mm});
            skLineSegment(sketch, "E79.16", {"start": v(80, -80) * mm, "end": v(80, 80) * mm});
            skArc(sketch, "E79.17", {"start": v(70, -90) * mm, "mid": v(77.07, -87.07) * mm, "end": v(80, -80) * mm});
            skLineSegment(sketch, "E79.18", {"start": v(-70, -90) * mm, "end": v(70, -90) * mm});
            skArc(sketch, "E79.19", {"start": v(-80, -80) * mm, "mid": v(-77.07, -87.07) * mm, "end": v(-70, -90) * mm});
            skPoint(sketch, "E79.20", {"position": v(58.99, 44.68) * mm});
            skPoint(sketch, "E79.21", {"position": v(58.99, -44.68) * mm});
            skPoint(sketch, "E79.22", {"position": v(-77.07, 87.07) * mm});
            skPoint(sketch, "E79.23", {"position": v(77.07, 87.07) * mm});
            skPoint(sketch, "E80.endSnap0", {"position": v(0, 90) * mm});
            skLineSegment(sketch, "E81", {"start": v(-37.8, 90) * mm, "end": v(-15.65, 108) * mm});
            skLineSegment(sketch, "E82", {"start": v(-15.65, 108) * mm, "end": v(-15.65, 120.16) * mm});
            skLineSegment(sketch, "E83", {"start": v(32.35, 90) * mm, "end": v(14.35, 108) * mm});
            skLineSegment(sketch, "E84", {"start": v(14.35, 108) * mm, "end": v(14.35, 120) * mm});
            skCircle(sketch, "E85", {"center": v(0, 120.16) * mm, "radius": 6 * mm});
            skArc(sketch, "E86", {"start": v(14.35, 120) * mm, "mid": v(-0.57, 135) * mm, "end": v(-15.65, 120.16) * mm});
            skLineSegment(sketch, "E87", {"start": v(0, 120.16) * mm, "end": v(0, 90) * mm, "construction": true});
            skLineSegment(sketch, "E88", {"start": v(80, 0) * mm, "end": v(-80, 0) * mm, "construction": true});
            skLineSegment(sketch, "E89.MirrorCS", {"start": v(-37.8, -90) * mm, "end": v(-15.65, -108) * mm});
            skLineSegment(sketch, "E90.MirrorCS", {"start": v(-15.65, -108) * mm, "end": v(-15.65, -120.16) * mm});
            skArc(sketch, "E91.MirrorCS", {"start": v(14.35, -120) * mm, "mid": v(-0.57, -135) * mm, "end": v(-15.65, -120.16) * mm});
            skCircle(sketch, "E92.MirrorC", {"center": v(0, -120.16) * mm, "radius": 6 * mm});
            skLineSegment(sketch, "E93.MirrorCS", {"start": v(0, -120.16) * mm, "end": v(0, -90) * mm, "construction": true});
            skLineSegment(sketch, "E94.MirrorCS", {"start": v(32.35, -90) * mm, "end": v(14.35, -108) * mm});
            skLineSegment(sketch, "E95.MirrorCS", {"start": v(14.35, -108) * mm, "end": v(14.35, -120) * mm});
            skSolve(sketch);
        }
        {
            var Q0;
            Q0=makeQuery(id+"F16.imprint","IMPRINT",FACE,{"disambiguationData":[TD([[makeQuery(id+"F16.imprint","IMPRINT",EDGE,{"derivedFrom":sQuery(id+"F16.wireOp",EDGE,"E79.0")}),-1.0]])]});
            var Q1;
            {var subQ1=sQuery(id+"F16.wireOp",EDGE,"E81");Q1=makeQuery(id+"F16.imprint","IMPRINT",FACE,{"disambiguationData":[TD([[makeQuery(id+"F16.imprint","IMPRINT",EDGE,{"derivedFrom":subQ1}),-1.0]])]});}
            var Q2;
            {var subQ0=sQuery(id+"F16.wireOp",EDGE,"E89.MirrorCS");Q2=makeQuery(id+"F16.imprint","IMPRINT",FACE,{"disambiguationData":[TD([[makeQuery(id+"F16.imprint","IMPRINT",EDGE,{"derivedFrom":subQ0}),1.0]])]});}
            var Q3;
            Q3=makeQuery(id+"F2.opExtrude","CAP_FACE",FACE,{"disambiguationData":[OSD([sQuery(id+"F0.wireOp",EDGE,"E12"),sQuery(id+"F0.wireOp",EDGE,"E13"),sQuery(id+"F0.wireOp",EDGE,"E14"),sQuery(id+"F0.wireOp",EDGE,"E15"),sQuery(id+"F0.wireOp",EDGE,"E17.filletArc"),sQuery(id+"F0.wireOp",EDGE,"E18.filletArc"),sQuery(id+"F0.wireOp",EDGE,"E19.filletArc"),sQuery(id+"F0.wireOp",EDGE,"E20.filletArc"),sQuery(id+"F0.wireOp",EDGE,"E25.0"),sQuery(id+"F0.wireOp",EDGE,"E25.1"),sQuery(id+"F0.wireOp",EDGE,"E25.2"),sQuery(id+"F0.wireOp",EDGE,"E25.3"),sQuery(id+"F0.wireOp",EDGE,"E25.4"),sQuery(id+"F0.wireOp",EDGE,"E25.5"),sQuery(id+"F0.wireOp",EDGE,"E25.6"),sQuery(id+"F0.wireOp",EDGE,"E25.7")])],"isStart":false});
            extrude(context, id + "F17", {"entities" : qUnion([Q0, Q1, Q2]), "endBound" : BoundingType.UP_TO_SURFACE, "endBoundEntityFace" : qUnion([Q3]), "depth" : 25 * mm});
        }
    });
